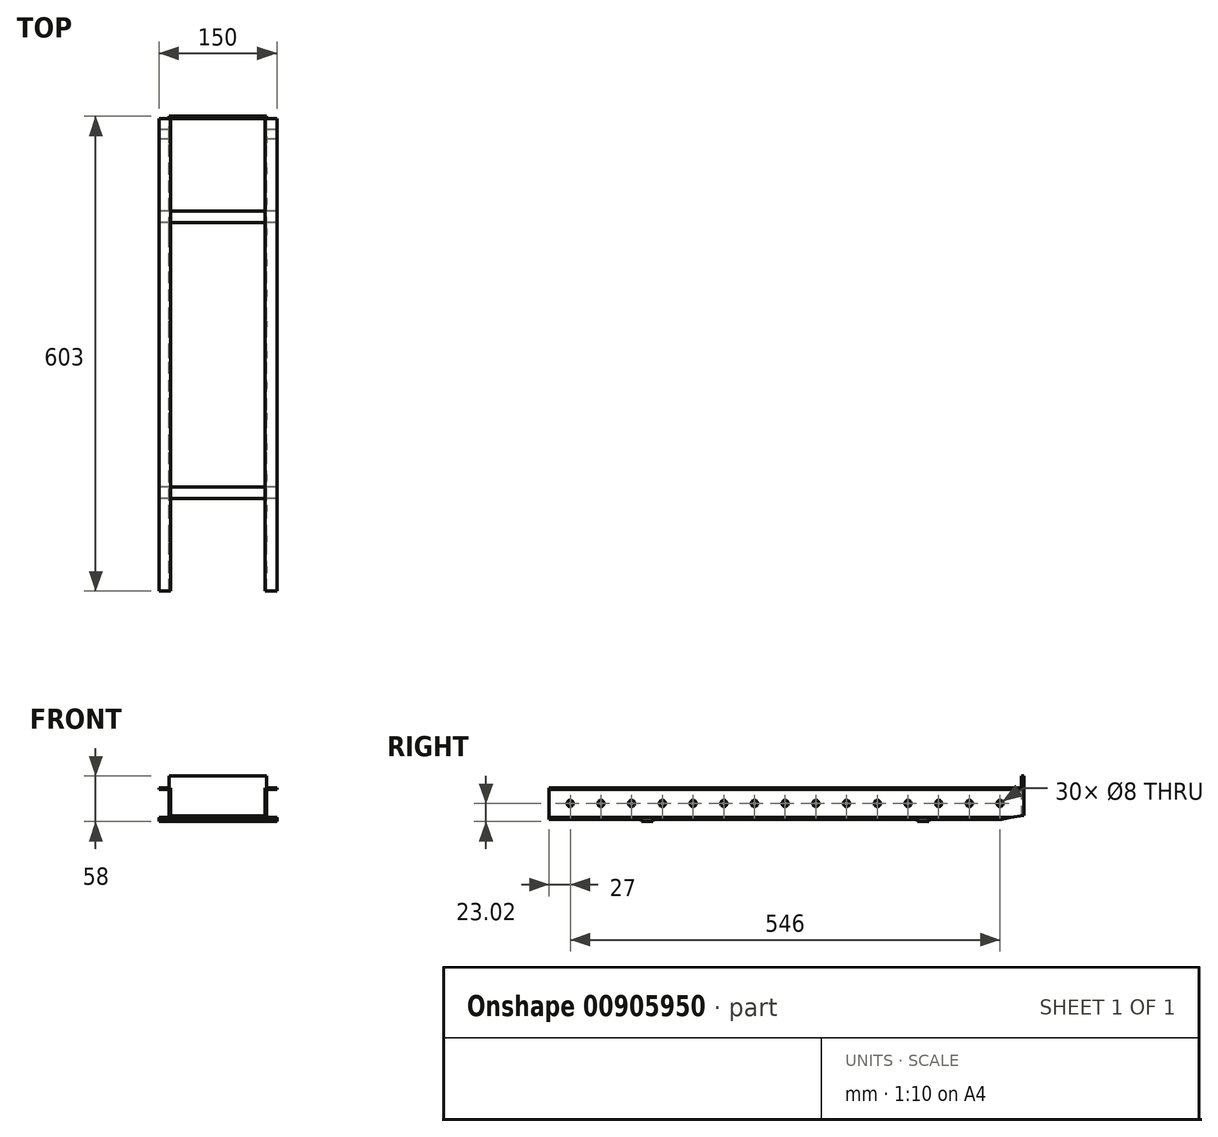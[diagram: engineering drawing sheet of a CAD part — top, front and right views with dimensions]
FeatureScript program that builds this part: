
annotation { "Feature Type Name" : "Feature", "Feature Type Description" : "" }
export const myFeature = defineFeature(function(context is Context, id is Id, definition is map)
    precondition{}
    {
        {
            var Q0;
            Q0=qCreatedBy(makeId("Front.planeOp"),FACE);
            var sketch = newSketch(context, id + "F0", { "sketchPlane" : qUnion([Q0])});
            skLineSegment(sketch, "E0.right", {"start": v(75, 19.54) * mm, "end": v(75, 17.54) * mm});
            skPoint(sketch, "E0.middle", {"position": v(0, 0) * mm});
            skLineSegment(sketch, "E1.bottom", {"start": v(75, 17.54) * mm, "end": v(62, 17.54) * mm});
            skLineSegment(sketch, "E1.top", {"start": v(75, -18.46) * mm, "end": v(62, -18.46) * mm});
            skLineSegment(sketch, "E1.right", {"start": v(62, 17.54) * mm, "end": v(62, -18.46) * mm});
            skLineSegment(sketch, "E2.trimOffspring", {"start": v(75, -18.46) * mm, "end": v(75, -20.46) * mm});
            skLineSegment(sketch, "E3", {"start": v(75, 19.54) * mm, "end": v(60, 19.54) * mm});
            skLineSegment(sketch, "E4", {"start": v(60, 19.54) * mm, "end": v(60, -20.46) * mm});
            skLineSegment(sketch, "E5", {"start": v(60, -20.46) * mm, "end": v(75, -20.46) * mm});
            skLineSegment(sketch, "E6.MirrorCS", {"start": v(-75, -18.46) * mm, "end": v(-75, -20.46) * mm});
            skLineSegment(sketch, "E7.MirrorCS", {"start": v(-75, 19.54) * mm, "end": v(-75, 17.54) * mm});
            skLineSegment(sketch, "E8.MirrorCS", {"start": v(-60, 19.54) * mm, "end": v(-60, -20.46) * mm});
            skLineSegment(sketch, "E9.MirrorCS", {"start": v(-75, 19.54) * mm, "end": v(-60, 19.54) * mm});
            skLineSegment(sketch, "E10.MirrorCS", {"start": v(-75, 17.54) * mm, "end": v(-62, 17.54) * mm});
            skLineSegment(sketch, "E11.MirrorCS", {"start": v(-60, -20.46) * mm, "end": v(-75, -20.46) * mm});
            skLineSegment(sketch, "E12.MirrorCS", {"start": v(-75, -18.46) * mm, "end": v(-62, -18.46) * mm});
            skLineSegment(sketch, "E13.MirrorCS", {"start": v(-62, 17.54) * mm, "end": v(-62, -18.46) * mm});
            skSolve(sketch);
        }
        {
            var Q0;
            Q0 = qSketchRegion(id + "F0", true);
            extrude(context, id + "F1", {"entities" : qUnion([Q0]), "depth" : 600 * mm, "offsetDistance" : 25 * mm});
        }
        {
            var Q0;
            Q0=makeQuery(id+"F1.opExtrude","SWEPT_FACE",FACE,{"disambiguationData":[OSD([sQuery(id+"F0.wireOp",EDGE,"E1.right")])]});
            var sketch = newSketch(context, id + "F2", { "sketchPlane" : qUnion([Q0])});
            skLineSegment(sketch, "E14", {"start": v(-600, -0.46) * mm, "end": v(0, 0) * mm, "construction": true});
            skCircle(sketch, "E15", {"center": v(-573, -0.44) * mm, "radius": 4 * mm});
            skCircle(sketch, "E16.1.0.0", {"center": v(-534, -0.44) * mm, "radius": 4 * mm});
            skCircle(sketch, "E16.2.0.0", {"center": v(-495, -0.44) * mm, "radius": 4 * mm});
            skCircle(sketch, "E16.3.0.0", {"center": v(-456, -0.44) * mm, "radius": 4 * mm});
            skCircle(sketch, "E16.4.0.0", {"center": v(-417, -0.44) * mm, "radius": 4 * mm});
            skCircle(sketch, "E16.5.0.0", {"center": v(-378, -0.44) * mm, "radius": 4 * mm});
            skCircle(sketch, "E16.6.0.0", {"center": v(-339, -0.44) * mm, "radius": 4 * mm});
            skCircle(sketch, "E16.7.0.0", {"center": v(-300, -0.44) * mm, "radius": 4 * mm});
            skCircle(sketch, "E16.8.0.0", {"center": v(-261, -0.44) * mm, "radius": 4 * mm});
            skCircle(sketch, "E16.9.0.0", {"center": v(-222, -0.44) * mm, "radius": 4 * mm});
            skCircle(sketch, "E16.10.0.0", {"center": v(-183, -0.44) * mm, "radius": 4 * mm});
            skCircle(sketch, "E16.11.0.0", {"center": v(-144, -0.44) * mm, "radius": 4 * mm});
            skCircle(sketch, "E16.12.0.0", {"center": v(-105, -0.44) * mm, "radius": 4 * mm});
            skCircle(sketch, "E16.13.0.0", {"center": v(-66, -0.44) * mm, "radius": 4 * mm});
            skCircle(sketch, "E16.14.0.0", {"center": v(-27, -0.44) * mm, "radius": 4 * mm});
            skLineSegment(sketch, "E16.direction1", {"start": v(-573, -0.44) * mm, "end": v(-534, -0.44) * mm, "construction": true});
            skSolve(sketch);
        }
        {
            var Q0;
            Q0 = qSketchRegion(id + "F2", true);
            var Q1;
            Q1=makeQuery(id+"F1.opExtrude","SWEPT_FACE",FACE,{"disambiguationData":[OSD([sQuery(id+"F0.wireOp",EDGE,"E13.MirrorCS")])]});
            extrude(context, id + "F3", {"entities" : qUnion([Q0]), "operationType" : NewBodyOperationType.REMOVE, "endBound" : BoundingType.UP_TO_SURFACE, "oppositeDirection" : true, "depth" : 25 * mm, "endBoundEntityFace" : qUnion([Q1]), "offsetDistance" : 25 * mm});
        }
        {
            var Q0;
            Q0=makeQuery(id+"F1.opExtrude","CAP_FACE",FACE,{"disambiguationData":[OSD([sQuery(id+"F0.wireOp",EDGE,"E0.right"),sQuery(id+"F0.wireOp",EDGE,"E1.bottom"),sQuery(id+"F0.wireOp",EDGE,"E1.top"),sQuery(id+"F0.wireOp",EDGE,"E1.right"),sQuery(id+"F0.wireOp",EDGE,"E2.trimOffspring"),sQuery(id+"F0.wireOp",EDGE,"E3"),sQuery(id+"F0.wireOp",EDGE,"E4"),sQuery(id+"F0.wireOp",EDGE,"E5")])],"isStart":true});
            var sketch = newSketch(context, id + "F4", { "sketchPlane" : qUnion([Q0])});
            skLineSegment(sketch, "E17.bottom", {"start": v(-62, 34.54) * mm, "end": v(62, 34.54) * mm});
            skLineSegment(sketch, "E17.top", {"start": v(-62, -20.46) * mm, "end": v(62, -20.46) * mm});
            skLineSegment(sketch, "E17.left", {"start": v(-62, 34.54) * mm, "end": v(-62, -20.46) * mm});
            skLineSegment(sketch, "E17.right", {"start": v(62, 34.54) * mm, "end": v(62, -20.46) * mm});
            skSolve(sketch);
        }
        {
            var Q0;
            Q0=makeQuery(id+"F1.opExtrude","SWEPT_FACE",FACE,{"disambiguationData":[OSD([sQuery(id+"F0.wireOp",EDGE,"E5")])]});
            var sketch = newSketch(context, id + "F5", { "sketchPlane" : qUnion([Q0])});
            skLineSegment(sketch, "E18", {"start": v(60, 300) * mm, "end": v(-61.14, 300) * mm, "construction": true});
            skLineSegment(sketch, "E19.bottom", {"start": v(75, 482.73) * mm, "end": v(-75, 482.73) * mm});
            skLineSegment(sketch, "E19.top", {"start": v(75, 467.73) * mm, "end": v(-75, 467.73) * mm});
            skLineSegment(sketch, "E19.left", {"start": v(75, 482.73) * mm, "end": v(75, 467.73) * mm});
            skLineSegment(sketch, "E19.right", {"start": v(-75, 482.73) * mm, "end": v(-75, 467.73) * mm});
            skLineSegment(sketch, "E20.MirrorCS", {"start": v(-75, 117.27) * mm, "end": v(-75, 132.27) * mm});
            skLineSegment(sketch, "E21.MirrorCS", {"start": v(75, 132.27) * mm, "end": v(-75, 132.27) * mm});
            skLineSegment(sketch, "E22.MirrorCS", {"start": v(75, 117.27) * mm, "end": v(-75, 117.27) * mm});
            skLineSegment(sketch, "E23.MirrorCS", {"start": v(75, 117.27) * mm, "end": v(75, 132.27) * mm});
            skSolve(sketch);
        }
        {
            var Q0;
            Q0 = qSketchRegion(id + "F5", true);
            extrude(context, id + "F6", {"entities" : qUnion([Q0]), "operationType" : NewBodyOperationType.ADD, "depth" : 3 * mm, "offsetDistance" : 25 * mm});
        }
        {
            var Q0;
            Q0 = qSketchRegion(id + "F4", true);
            extrude(context, id + "F7", {"entities" : qUnion([Q0]), "operationType" : NewBodyOperationType.ADD, "depth" : 3 * mm, "offsetDistance" : 25 * mm});
        }
        {
            var Q0;
            Q0=makeQuery(id+"F7.opExtrude","CAP_EDGE",EDGE,{"disambiguationData":[OSD([sQuery(id+"F4.wireOp",EDGE,"E17.top")])],"isStart":false});
            chamfer(context, id + "F8", {"entities" : qUnion([Q0]), "chamferType" : ChamferType.OFFSET_ANGLE, "width" : 5 * mm, "oppositeDirection" : false, "angle" : 80 * degree, "tangentPropagation" : true});
        }
    });
